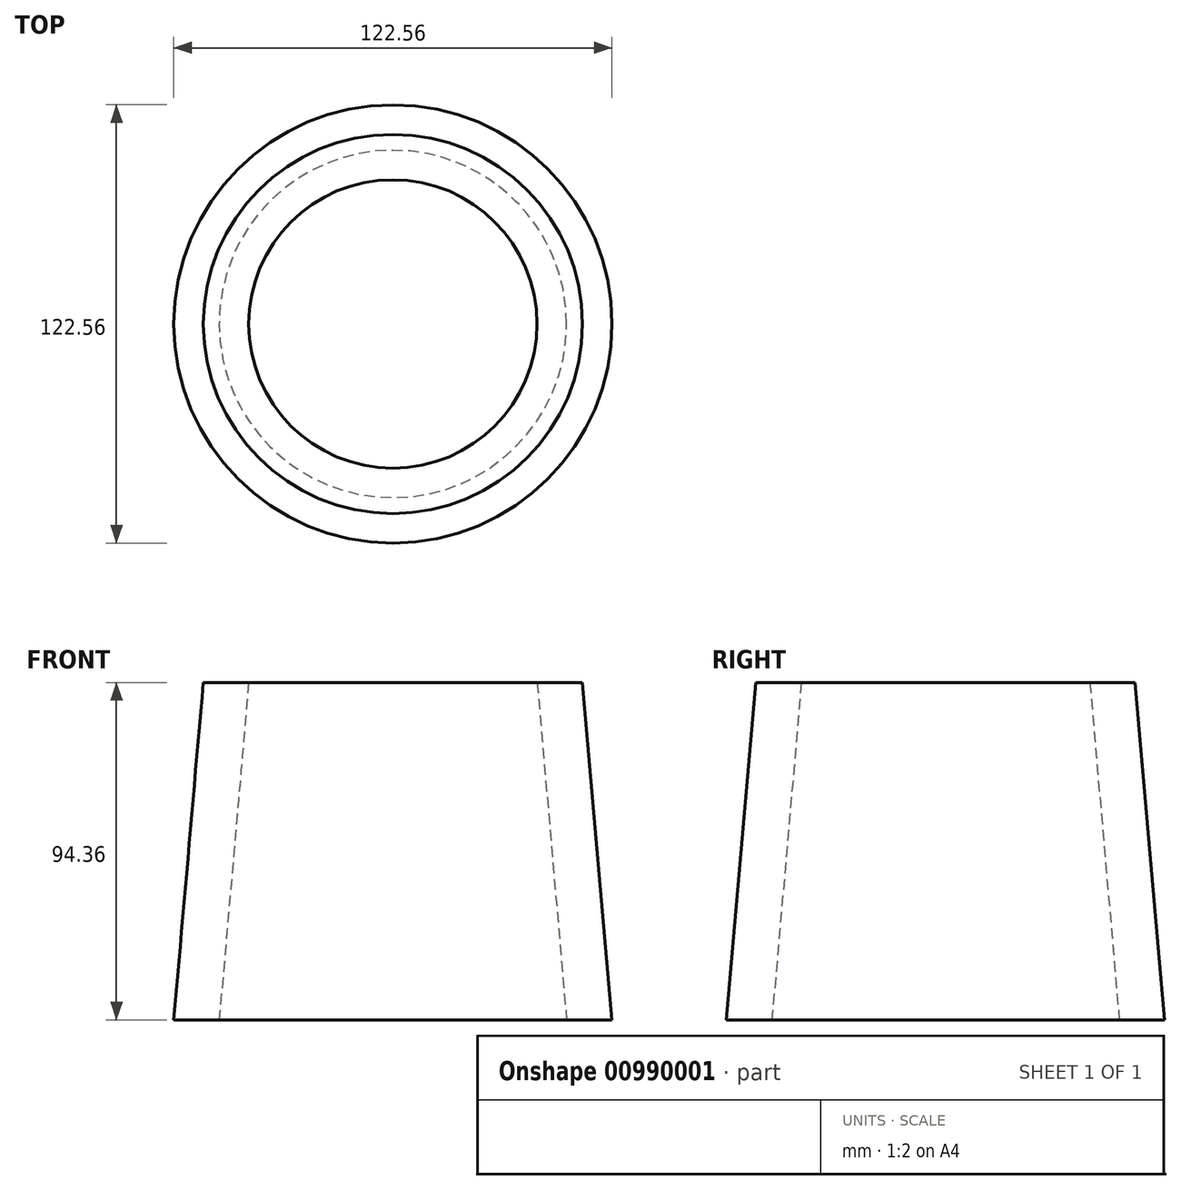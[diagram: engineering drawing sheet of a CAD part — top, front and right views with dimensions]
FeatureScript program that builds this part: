
annotation { "Feature Type Name" : "Feature", "Feature Type Description" : "" }
export const myFeature = defineFeature(function(context is Context, id is Id, definition is map)
    precondition{}
    {
        {
            var Q0;
            Q0=qCreatedBy(makeId("Front.planeOp"),FACE);
            var sketch = newSketch(context, id + "F0", { "sketchPlane" : qUnion([Q0])});
            skLineSegment(sketch, "E0", {"start": v(-63.5, 0) * mm, "end": v(0, 0) * mm});
            skLineSegment(sketch, "E1", {"start": v(0, 0) * mm, "end": v(0, 25.4) * mm});
            skLineSegment(sketch, "E2", {"start": v(0, 25.4) * mm, "end": v(-61.28, 25.4) * mm});
            skLineSegment(sketch, "E3", {"start": v(-61.28, 25.4) * mm, "end": v(-63.5, 0) * mm});
            skLineSegment(sketch, "E4", {"start": v(0, 0) * mm, "end": v(0, 30.51) * mm, "construction": true});
            skLineSegment(sketch, "E5", {"start": v(-61.28, 25.4) * mm, "end": v(-48.58, 25.4) * mm});
            skLineSegment(sketch, "E6", {"start": v(-48.58, 25.4) * mm, "end": v(-40.32, 119.76) * mm});
            skLineSegment(sketch, "E7", {"start": v(-40.32, 119.76) * mm, "end": v(-53.02, 119.76) * mm});
            skLineSegment(sketch, "E8", {"start": v(-53.02, 119.76) * mm, "end": v(-61.28, 25.4) * mm});
            skLineSegment(sketch, "E9", {"start": v(-53.02, 119.76) * mm, "end": v(-50.8, 145.16) * mm});
            skLineSegment(sketch, "E10", {"start": v(-50.8, 145.16) * mm, "end": v(0, 145.16) * mm});
            skLineSegment(sketch, "E11", {"start": v(0, 145.16) * mm, "end": v(0, 119.76) * mm});
            skLineSegment(sketch, "E12", {"start": v(0, 119.76) * mm, "end": v(-40.32, 119.76) * mm});
            skSolve(sketch);
        }
        {
            var Q0;
            {var subQ2=sQuery(id+"F0.wireOp",EDGE,"E6");Q0=makeQuery(id+"F0.imprint","IMPRINT",FACE,{"disambiguationData":[TD([[makeQuery(id+"F0.imprint","IMPRINT",EDGE,{"derivedFrom":subQ2}),1.0]])]});}
            var Q1;
            Q1=sQuery(id+"F0.wireOp",EDGE,"E1");
            revolve(context, id + "F1", {"surfaceOperationType" : NewSurfaceOperationType.NEW, "entities" : qUnion([Q0]), "axis" : qUnion([Q1]), "revolveType" : RevolveType.FULL});
        }
    });
